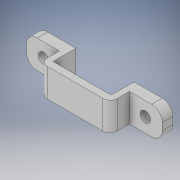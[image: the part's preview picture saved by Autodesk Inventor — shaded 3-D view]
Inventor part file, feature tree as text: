
AUTODESK INVENTOR PART (.ipt)
format: ipt  version: 2018 (Build 220112000, 112)  size: 176,640 bytes
history: native  units: in
note: dims shown in document units (in); Inventor stores cm internally (conversion verified against a paired STEP export)
features: extrude x5, sketch x5, fillet x2, shell x1
ambient origin geometry x8: Origin, YZ Plane, XZ Plane, XY Plane, X Axis, Y Axis, Z Axis, Center Point
bodies: Solid1 (feature_tree)
feature tree (13):
  extrude  "Extrusion1"  Depth=0.6496in
  shell  "Shell1"  Thickness=0.2559in
  extrude  "Extrusion2"  TaperAngle=0.0deg  [1 undecoded]
  extrude  "Extrusion3"  Depth=0.315in
  fillet  "Fillet1"  [1 undecoded]
  extrude  "Extrusion4"  Depth=0.315in
  extrude  "Extrusion6"  Depth=0.0787in
  fillet  "Fillet3"  Radius=0.5679in
  sketch  "Sketch1"  dims[d0=0.315in d1=0.6496in d2=0.2559in d3=0.0in]
  sketch  "Sketch2"  dims[d4=0.1181in d5=0.0in]
  sketch  "Sketch3"  dims[d6=0.315in d7=0.315in d8=0.0in]
  sketch  "Sketch4"  dims[d9=0.315in d10=0.315in]
  sketch  "Sketch6"  dims[d11=0.1181in d12=0.0in d13=1.1358in d14=0.5679in d15=0.5679in d16=0.1181in d17=0.1181in d18=0.1969in d19=0.0in d20=0.1181in d25=0.3543in d26=0.315in d27=0.315in d28=0.3543in d29=1.0in d30=0.0in d33=0.0394in d34=0.0in d35=0.0787in]
note: 2 required parameter values undecoded (feature->parameter linkage not recoverable at this tier; creation-order binding heuristic only, values carry confidence <= 0.55)
